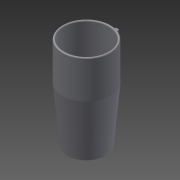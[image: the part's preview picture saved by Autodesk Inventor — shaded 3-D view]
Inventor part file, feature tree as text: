
AUTODESK INVENTOR PART (.ipt)
format: ipt  version: 2014 SP1 (Build 180222100, 222)  size: 127,488 bytes
history: native  units: mm
features: sketch x3, extrude x2, plane x2, loft x1, shell x1, fillet x1, other x1
ambient origin geometry x8: Origin, YZ Plane, XZ Plane, XY Plane, X Axis, Y Axis, Z Axis, Center Point
bodies: Solid1 (feature_tree)
feature tree (11):
  extrude  "Extrusion1"  Depth=55.0mm TaperAngle=0.0deg
  plane  "Work Plane1"
  loft  "Loft1"
  shell  "Shell1"  Thickness=0.0mm
  plane  "Work Plane3"
  extrude  "Extrusion2"  Depth=1.5mm
  fillet  "Fillet1"  Radius=35.0mm
  sketch  "Sketch1"  dims[d0=70.0mm d1=55.0mm d2=0.0mm]
  sketch  "Sketch2"  dims[d3=-80.0mm d4=56.0mm d5=0.0mm d6=90.0deg]
  other  "Edges1"
  sketch  "Sketch3"  dims[d7=0.0mm d8=90.0deg d9=3.0mm d11=35.0mm d15=5.0mm d18=5.0mm d19=10.0mm d20=0.0mm d21=1.5mm]
